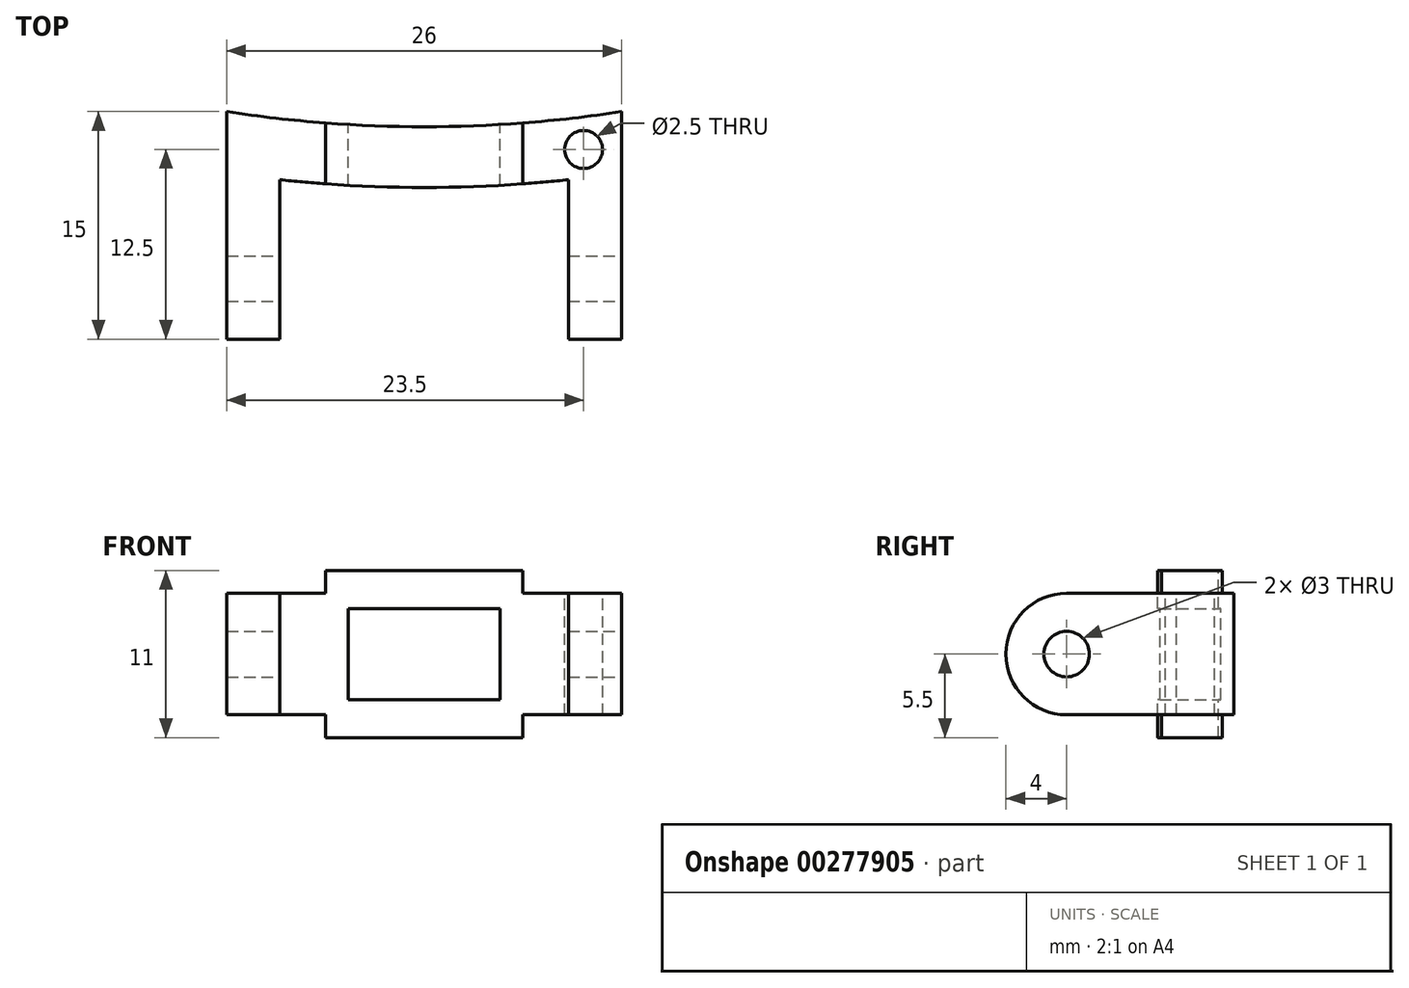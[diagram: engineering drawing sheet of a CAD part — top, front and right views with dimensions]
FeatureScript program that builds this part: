
annotation { "Feature Type Name" : "Feature", "Feature Type Description" : "" }
export const myFeature = defineFeature(function(context is Context, id is Id, definition is map)
    precondition{}
    {
        {
            var Q0;
            Q0=qCreatedBy(makeId("Front.planeOp"),FACE);
            var sketch = newSketch(context, id + "F0", { "sketchPlane" : qUnion([Q0])});
            skLineSegment(sketch, "E0.bottom", {"start": v(5, -3) * mm, "end": v(-5, -3) * mm});
            skLineSegment(sketch, "E0.top", {"start": v(5, 3) * mm, "end": v(-5, 3) * mm});
            skLineSegment(sketch, "E0.left", {"start": v(5, -3) * mm, "end": v(5, 3) * mm});
            skLineSegment(sketch, "E0.right", {"start": v(-5, -3) * mm, "end": v(-5, 3) * mm});
            skPoint(sketch, "E0.middle", {"position": v(0, 0) * mm});
            skLineSegment(sketch, "E1.bottom", {"start": v(6.5, -5.5) * mm, "end": v(-6.5, -5.5) * mm});
            skLineSegment(sketch, "E1.top", {"start": v(6.5, 5.5) * mm, "end": v(-6.5, 5.5) * mm});
            skLineSegment(sketch, "E1.left", {"start": v(13, -4) * mm, "end": v(13, 4) * mm});
            skLineSegment(sketch, "E1.right", {"start": v(-13, -4) * mm, "end": v(-13, 4) * mm});
            skLineSegment(sketch, "E2", {"start": v(6.5, 5.5) * mm, "end": v(6.5, 4) * mm});
            skLineSegment(sketch, "E3", {"start": v(6.5, 4) * mm, "end": v(13, 4) * mm});
            skLineSegment(sketch, "E4", {"start": v(0, 0) * mm, "end": v(13, 0) * mm, "construction": true});
            skLineSegment(sketch, "E5.MirrorCS", {"start": v(6.5, -5.5) * mm, "end": v(6.5, -4) * mm});
            skLineSegment(sketch, "E6.MirrorCS", {"start": v(6.5, -4) * mm, "end": v(13, -4) * mm});
            skLineSegment(sketch, "E7", {"start": v(0, 0) * mm, "end": v(0, 5.5) * mm, "construction": true});
            skLineSegment(sketch, "E8.MirrorCS", {"start": v(-6.5, 5.5) * mm, "end": v(-6.5, 4) * mm});
            skLineSegment(sketch, "E9.MirrorCS", {"start": v(-6.5, 4) * mm, "end": v(-13, 4) * mm});
            skLineSegment(sketch, "E10.MirrorCS", {"start": v(-6.5, -4) * mm, "end": v(-13, -4) * mm});
            skLineSegment(sketch, "E11.MirrorCS", {"start": v(-6.5, -5.5) * mm, "end": v(-6.5, -4) * mm});
            skPoint(sketch, "E12.orphan", {"position": v(-13, 5.5) * mm});
            skPoint(sketch, "E13.orphan", {"position": v(-13, -5.5) * mm});
            skPoint(sketch, "E14.orphan", {"position": v(13, -5.5) * mm});
            skPoint(sketch, "E15.orphan", {"position": v(13, 5.5) * mm});
            skSolve(sketch);
        }
        {
            var Q0;
            Q0 = qSketchRegion(id + "F0", true);
            extrude(context, id + "F1", {"entities" : qUnion([Q0]), "depth" : 15 * mm});
        }
        {
            var Q0;
            Q0=qCreatedBy(makeId("Top.planeOp"),FACE);
            var sketch = newSketch(context, id + "F2", { "sketchPlane" : qUnion([Q0])});
            skLineSegment(sketch, "E16", {"start": v(-3.15, -1) * mm, "end": v(1.9, -1) * mm, "construction": true});
            skLineSegment(sketch, "E17", {"start": v(-3.09, -5) * mm, "end": v(1.78, -5) * mm, "construction": true});
            skArc(sketch, "E18", {"start": v(-13, 0) * mm, "mid": v(0, -1) * mm, "end": v(13, 0) * mm});
            skArc(sketch, "E19", {"start": v(-9.5, -4.5) * mm, "mid": v(0, -5) * mm, "end": v(9.5, -4.5) * mm});
            skLineSegment(sketch, "E20", {"start": v(-9.5, -4.5) * mm, "end": v(-9.5, -15) * mm});
            skLineSegment(sketch, "E21", {"start": v(-9.5, -15) * mm, "end": v(9.5, -15) * mm});
            skLineSegment(sketch, "E22", {"start": v(9.5, -15) * mm, "end": v(9.5, -4.5) * mm});
            skLineSegment(sketch, "E23", {"start": v(0, 0) * mm, "end": v(0, -15) * mm, "construction": true});
            skLineSegment(sketch, "E24", {"start": v(-13, 0) * mm, "end": v(13, 0) * mm});
            skSolve(sketch);
        }
        {
            var Q0;
            Q0 = qSketchRegion(id + "F2", true);
            extrude(context, id + "F3", {"entities" : qUnion([Q0]), "operationType" : NewBodyOperationType.REMOVE, "endBound" : BoundingType.THROUGH_ALL, "oppositeDirection" : true, "depth" : 25 * mm, "hasSecondDirection" : true, "secondDirectionBound" : BoundingType.THROUGH_ALL, "secondDirectionOppositeDirection" : false, "secondDirectionDepth" : 25 * mm});
        }
        {
            var Q0;
            Q0=qCreatedBy(makeId("Right.planeOp"),FACE);
            var sketch = newSketch(context, id + "F4", { "sketchPlane" : qUnion([Q0])});
            skCircle(sketch, "E25", {"center": v(-11, 0) * mm, "radius": 1.5 * mm});
            skArc(sketch, "E26", {"start": v(-11, 4) * mm, "mid": v(-15, 0) * mm, "end": v(-11, -4) * mm});
            skLineSegment(sketch, "E27", {"start": v(-11, 4) * mm, "end": v(-15, 4) * mm});
            skLineSegment(sketch, "E28", {"start": v(-15, 4) * mm, "end": v(-15, -4) * mm});
            skLineSegment(sketch, "E29", {"start": v(-15, -4) * mm, "end": v(-11, -4) * mm});
            skSolve(sketch);
        }
        {
            var Q0;
            Q0 = qSketchRegion(id + "F4", true);
            extrude(context, id + "F5", {"entities" : qUnion([Q0]), "operationType" : NewBodyOperationType.REMOVE, "endBound" : BoundingType.THROUGH_ALL, "oppositeDirection" : true, "depth" : 25 * mm, "hasSecondDirection" : true, "secondDirectionBound" : BoundingType.THROUGH_ALL, "secondDirectionOppositeDirection" : false, "secondDirectionDepth" : 25 * mm});
        }
        {
            var Q0;
            Q0=qCreatedBy(makeId("Top.planeOp"),FACE);
            var sketch = newSketch(context, id + "F6", { "sketchPlane" : qUnion([Q0])});
            skCircle(sketch, "E30", {"center": v(10.5, -2.5) * mm, "radius": 1.25 * mm});
            skSolve(sketch);
        }
        {
            var Q0;
            Q0 = qSketchRegion(id + "F6", true);
            extrude(context, id + "F7", {"entities" : qUnion([Q0]), "operationType" : NewBodyOperationType.REMOVE, "endBound" : BoundingType.THROUGH_ALL, "oppositeDirection" : true, "depth" : 25 * mm, "hasSecondDirection" : true, "secondDirectionBound" : BoundingType.THROUGH_ALL, "secondDirectionOppositeDirection" : false, "secondDirectionDepth" : 25 * mm});
        }
    });
